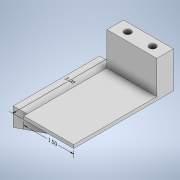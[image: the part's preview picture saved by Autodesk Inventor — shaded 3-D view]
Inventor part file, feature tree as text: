
AUTODESK INVENTOR PART (.ipt)
format: ipt  version: 2020 (Build 240168000, 168)  size: 145,920 bytes
history: native  units: in
note: dims shown in document units (in); Inventor stores cm internally (conversion verified against a paired STEP export)
features: sketch x4, other x3, extrude x3, hole x1, chamfer x1
ambient origin geometry x8: Origin, YZ Plane, XZ Plane, XY Plane, X Axis, Y Axis, Z Axis, Center Point
bodies: Solid1 (feature_tree)
feature tree (12):
  other  "Annotations"
  extrude  "Extrusion1"  Depth=3.0in
  extrude  "Extrusion2"  Depth=1.5in
  hole  "Hole1"  [1 undecoded]
  extrude  "Extrusion3"  Depth=0.5in
  chamfer  "Chamfer3"  Distance=0.4in
  sketch  "Sketch1"  dims[d0=1.5in d1=3.0in]
  sketch  "Sketch2"  dims[d2=0.1in d3=0.0in d4=1.5in]
  sketch  "Sketch6"  dims[d5=0.5in d6=1.0in d7=0.0in]
  sketch  "Sketch7"  dims[d8=0.375in d9=0.375in d10=0.2in d11=0.75in d12=0.75in d13=0.188in d14=0.5635in d15=0.5in d16=0.8108in d23=0.4in d24=0.2in d25=0.2in d26=1.62in d27=0.56in d28=0.0in d35=1.62in d36=0.56in d37=45.0deg d17=0.0in d18=0.3937in d19=1.5in d20=0.1641in d21=0.2363in d22=3.0in d29=0.5in d30=0.0344in]
  other  "Linear Dimension 1"
  other  "Linear Dimension 2"
note: 1 required parameter value undecoded (feature->parameter linkage not recoverable at this tier; creation-order binding heuristic only, values carry confidence <= 0.55)
